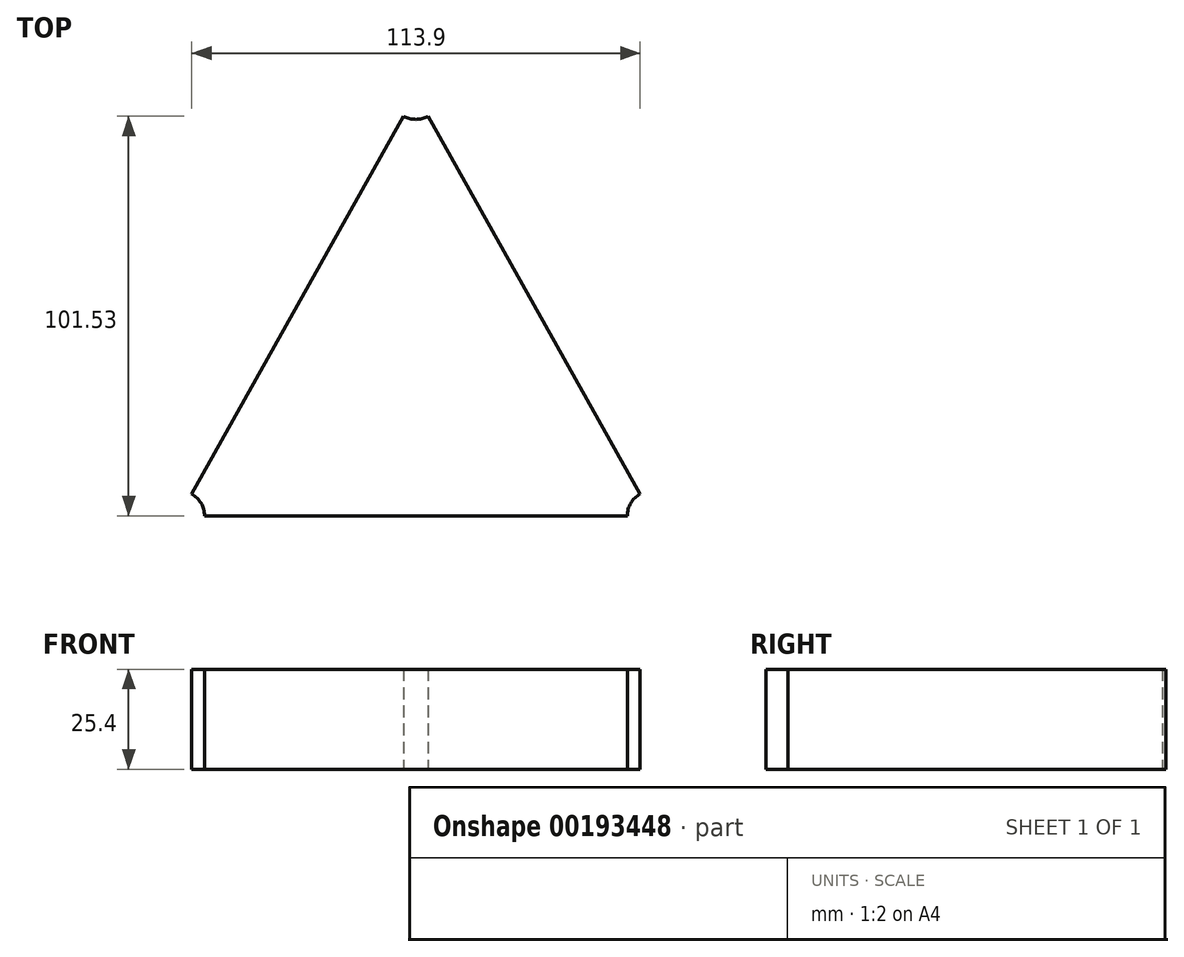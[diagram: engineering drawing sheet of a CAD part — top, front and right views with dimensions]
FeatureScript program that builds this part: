
annotation { "Feature Type Name" : "Feature", "Feature Type Description" : "" }
export const myFeature = defineFeature(function(context is Context, id is Id, definition is map)
    precondition{}
    {
        {
            var Q0;
            Q0=qCreatedBy(makeId("Top.planeOp"),FACE);
            var sketch = newSketch(context, id + "F0", { "sketchPlane" : qUnion([Q0])});
            skLineSegment(sketch, "E0", {"start": v(0, 0) * mm, "end": v(60.06, 107.07) * mm});
            skLineSegment(sketch, "E1", {"start": v(60.06, 107.07) * mm, "end": v(120.12, 0) * mm});
            skLineSegment(sketch, "E2", {"start": v(120.12, 0) * mm, "end": v(0, 0) * mm});
            skCircle(sketch, "E3", {"center": v(0, 0) * mm, "radius": 6.35 * mm});
            skCircle(sketch, "E4", {"center": v(120.12, 0) * mm, "radius": 6.35 * mm});
            skCircle(sketch, "E5", {"center": v(60.06, 107.07) * mm, "radius": 6.35 * mm});
            skSolve(sketch);
        }
        {
            var Q0;
            {var subQ0=sQuery(id+"F0.wireOp",EDGE,"E3");var subQ1=sQuery(id+"F0.wireOp",EDGE,"E0");var subQ2=makeQuery(id+"F0.imprint","INTERSECT",VERTEX,{"derivedFrom":[subQ1,subQ0]});Q0=makeQuery(id+"F0.imprint","IMPRINT",FACE,{"disambiguationData":[TD([[makeQuery(id+"F0.imprint","IMPRINT",EDGE,{"disambiguationData":[TD([[subQ2,-1.0]])],"derivedFrom":subQ1}),-1.0]])]});}
            extrude(context, id + "F1", {"entities" : qUnion([Q0]), "depth" : 25.4 * mm});
        }
    });
